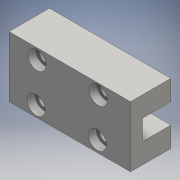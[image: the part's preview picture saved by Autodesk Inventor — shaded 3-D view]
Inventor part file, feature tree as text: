
AUTODESK INVENTOR PART (.ipt)
format: ipt  version: 2016 (Build 200138000, 138)  size: 122,880 bytes
history: native  units: mm
features: hole x4, extrude x2, sketch x2, other x1
ambient origin geometry x8: Origin, YZ Plane, XZ Plane, XY Plane, X Axis, Y Axis, Z Axis, Center Point
bodies: Body1 (feature_tree)
feature tree (9):
  other  "ソリッド1"
  extrude  "押し出し1"  Depth=30.0mm
  extrude  "押し出し2"  Depth=15.0mm
  hole  "穴1"  [1 undecoded]
  hole  "穴2"  [1 undecoded]
  hole  "穴3"  [1 undecoded]
  hole  "穴4"  [1 undecoded]
  sketch  "スケッチ1"
  sketch  "スケッチ2"
note: 4 required parameter values undecoded (feature->parameter linkage not recoverable at this tier; creation-order binding heuristic only, values carry confidence <= 0.55)
